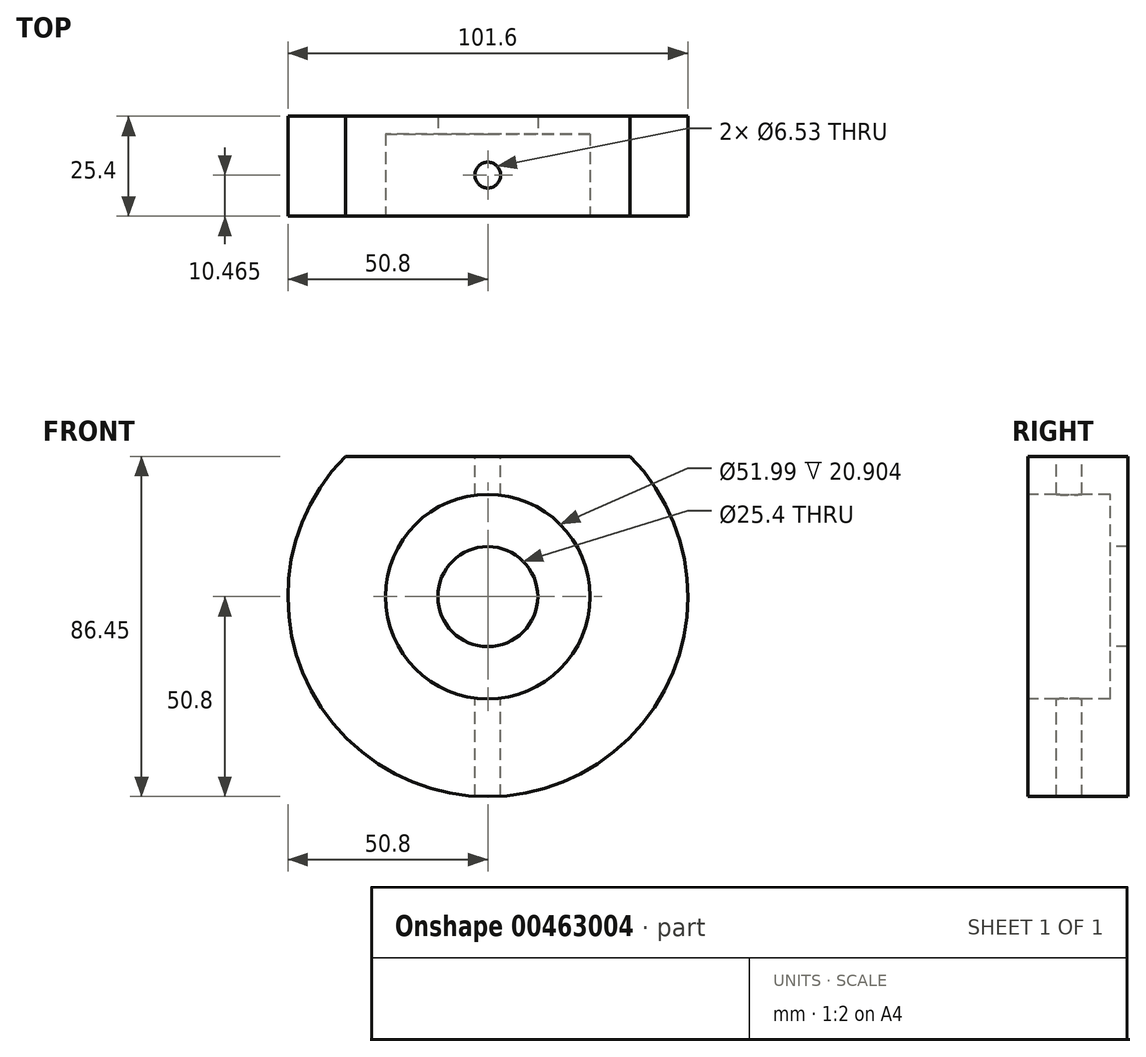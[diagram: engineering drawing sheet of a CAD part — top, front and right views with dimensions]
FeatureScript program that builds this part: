
annotation { "Feature Type Name" : "Feature", "Feature Type Description" : "" }
export const myFeature = defineFeature(function(context is Context, id is Id, definition is map)
    precondition{}
    {
        {
            var Q0;
            Q0=qCreatedBy(makeId("Front.planeOp"),FACE);
            var sketch = newSketch(context, id + "F0", { "sketchPlane" : qUnion([Q0])});
            skArc(sketch, "E0", {"start": v(-36.19, 35.65) * mm, "mid": v(0, -50.8) * mm, "end": v(36.19, 35.65) * mm});
            skLineSegment(sketch, "E1", {"start": v(-36.19, 35.65) * mm, "end": v(36.19, 35.65) * mm});
            skSolve(sketch);
        }
        {
            var Q0;
            Q0=makeQuery(id+"F0.imprint","IMPRINT",FACE,{"disambiguationData":[TD([[makeQuery(id+"F0.imprint","IMPRINT",EDGE,{"derivedFrom":sQuery(id+"F0.wireOp",EDGE,"E0")}),1.0]])]});
            extrude(context, id + "F1", {"entities" : qUnion([Q0]), "depth" : 25.4 * mm});
        }
        {
            var Q0;
            Q0=makeQuery(id+"F1.opExtrude","CAP_FACE",FACE,{"disambiguationData":[OSD([sQuery(id+"F0.wireOp",EDGE,"E0")])],"isStart":false});
            var sketch = newSketch(context, id + "F2", { "sketchPlane" : qUnion([Q0])});
            skPoint(sketch, "E2", {"position": v(0, 0) * mm});
            skCircle(sketch, "E3", {"center": v(0, 0) * mm, "radius": 26 * mm});
            skSolve(sketch);
        }
        {
            var Q0;
            Q0=makeQuery(id+"F2.imprint","IMPRINT",FACE,{"disambiguationData":[TD([[makeQuery(id+"F2.imprint","IMPRINT",EDGE,{"derivedFrom":makeQuery(id+"F1.opExtrude","CAP_EDGE",EDGE,{"disambiguationData":[OSD([sQuery(id+"F0.wireOp",EDGE,"E0")])],"isStart":false})}),1.0]])]});
            var sketch = newSketch(context, id + "F3", { "sketchPlane" : qUnion([Q0])});
            skCircle(sketch, "E4", {"center": v(0, 0) * mm, "radius": 26 * mm});
            skSolve(sketch);
        }
        {
            var Q0;
            Q0=makeQuery(id+"F3.imprint","IMPRINT",FACE,{"disambiguationData":[TD([[makeQuery(id+"F3.imprint","IMPRINT",EDGE,{"derivedFrom":sQuery(id+"F3.wireOp",EDGE,"E4")}),1.0]])]});
            extrude(context, id + "F4", {"entities" : qUnion([Q0]), "operationType" : NewBodyOperationType.ADD, "depth" : -20.9 * mm});
        }
        {
            var Q0;
            Q0=makeQuery(id+"F2.imprint","IMPRINT",FACE,{"disambiguationData":[TD([[makeQuery(id+"F2.imprint","IMPRINT",EDGE,{"derivedFrom":sQuery(id+"F2.wireOp",EDGE,"E3")}),1.0]])]});
            extrude(context, id + "F5", {"entities" : qUnion([Q0]), "operationType" : NewBodyOperationType.REMOVE, "oppositeDirection" : true, "depth" : 20.9 * mm});
        }
        {
            var Q0;
            Q0=makeQuery(id+"F5.boolean.opBoolean","COPY",FACE,{"derivedFrom":makeQuery(id+"F5.opExtrude","CAP_FACE",FACE,{"disambiguationData":[OSD([sQuery(id+"F2.wireOp",EDGE,"E3")])],"isStart":false})});
            var sketch = newSketch(context, id + "F6", { "sketchPlane" : qUnion([Q0])});
            skPoint(sketch, "E5", {"position": v(0, 0) * mm});
            skSolve(sketch);
        }
        {
            var Q0;
            Q0=sQuery(id+"F6.wireOp",VERTEX,"E5");
            var Q1;
            Q1=makeQuery(id+"F1.opExtrude","SWEPT_BODY",BODY,{"disambiguationData":[OSD([sQuery(id+"F0.wireOp",EDGE,"E0")])]});
            hole(context, id + "F7", {"style" : HoleStyle.SIMPLE, "endStyle" : HoleEndStyle.BLIND, "holeDiameter" : 25.4 * mm, "holeDepth" : 21 * mm, "isTappedThrough" : true, "tappedDepth" : 12.7 * mm, "tapClearance" : 3, "startFromSketch" : true, "locations" : qUnion([Q0]), "scope" : qUnion([Q1])});
        }
        {
            var Q0;
            Q0=makeQuery(id+"F1.opExtrude","CAP_FACE",FACE,{"disambiguationData":[OSD([sQuery(id+"F0.wireOp",EDGE,"E0")])],"isStart":false});
            var sketch = newSketch(context, id + "F8", { "sketchPlane" : qUnion([Q0])});
            skLineSegment(sketch, "E6", {"start": v(-34.63, 37.17) * mm, "end": v(34.63, 37.17) * mm});
            skSolve(sketch);
        }
        {
            var Q0;
            Q0=makeQuery(id+"F1.opExtrude","SWEPT_FACE",FACE,{"disambiguationData":[OSD([sQuery(id+"F0.wireOp",EDGE,"E1")])]});
            var sketch = newSketch(context, id + "F9", { "sketchPlane" : qUnion([Q0])});
            skPoint(sketch, "E7", {"position": v(0, -14.94) * mm});
            skSolve(sketch);
        }
        {
            var Q0;
            Q0=sQuery(id+"F9.wireOp",VERTEX,"E7");
            var Q1;
            Q1=makeQuery(id+"F1.opExtrude","SWEPT_BODY",BODY,{"disambiguationData":[OSD([sQuery(id+"F0.wireOp",EDGE,"E0"),sQuery(id+"F0.wireOp",EDGE,"E1")])]});
            hole(context, id + "F10", {"style" : HoleStyle.SIMPLE, "endStyle" : HoleEndStyle.THROUGH, "standardTappedOrClearance" : lookupTablePath({ "standard" : "ANSI", "engagement" : "75%", "pitch" : "18 tpi", "size" : "5/16", "type" : "Tapped" }), "standardBlindInLast" : lookupTablePath({ "standard" : "ANSI", "engagement" : "75%", "pitch" : "18 tpi", "size" : "5/16", "type" : "Tapped" }), "holeDiameter" : 6.53 * mm, "showTappedDepth" : true, "isTappedThrough" : true, "tappedDepth" : 12.7 * mm, "tapClearance" : 3, "locations" : qUnion([Q0]), "scope" : qUnion([Q1]), "majorDiameter" : 7.94 * mm});
        }
    });
